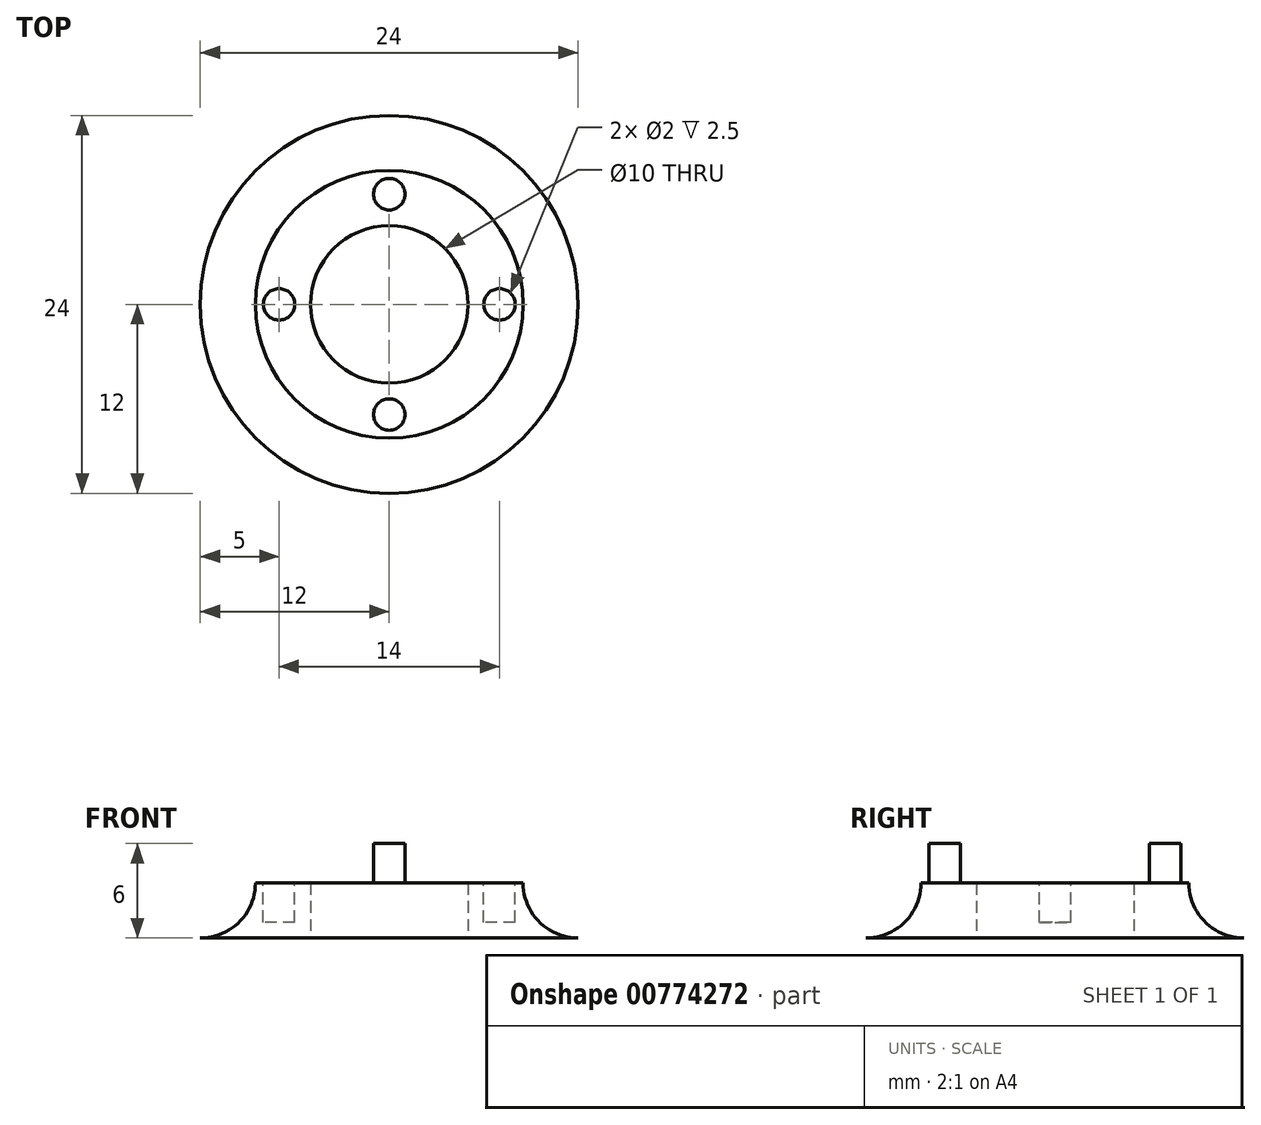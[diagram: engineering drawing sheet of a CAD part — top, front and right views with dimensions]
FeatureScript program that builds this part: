
annotation { "Feature Type Name" : "Feature", "Feature Type Description" : "" }
export const myFeature = defineFeature(function(context is Context, id is Id, definition is map)
    precondition{}
    {
        {
            var Q0;
            Q0=qCreatedBy(makeId("Front.planeOp"),FACE);
            var sketch = newSketch(context, id + "F0", { "sketchPlane" : qUnion([Q0])});
            skLineSegment(sketch, "E0.bottom", {"start": v(0, 0) * mm, "end": v(12, 0) * mm});
            skLineSegment(sketch, "E0.top", {"start": v(0, -3.5) * mm, "end": v(12, -3.5) * mm});
            skLineSegment(sketch, "E0.left", {"start": v(0, 0) * mm, "end": v(0, -3.5) * mm});
            skLineSegment(sketch, "E0.right", {"start": v(12, 0) * mm, "end": v(12, -3.5) * mm});
            skCircle(sketch, "E1", {"center": v(12, 0) * mm, "radius": 3.5 * mm});
            skLineSegment(sketch, "E2.bottom", {"start": v(0, 0) * mm, "end": v(5, 0) * mm});
            skLineSegment(sketch, "E2.top", {"start": v(0, -3.5) * mm, "end": v(5, -3.5) * mm});
            skLineSegment(sketch, "E2.right", {"start": v(5, 0) * mm, "end": v(5, -3.5) * mm});
            skLineSegment(sketch, "E3", {"start": v(0, 0) * mm, "end": v(0, 21.41) * mm});
            skSolve(sketch);
        }
        {
            var Q0;
            {var subQ0=sQuery(id+"F0.wireOp",EDGE,"E2.right");Q0=makeQuery(id+"F0.imprint","IMPRINT",FACE,{"disambiguationData":[TD([[makeQuery(id+"F0.imprint","IMPRINT",EDGE,{"derivedFrom":subQ0}),1.0]])]});}
            var Q1;
            Q1=sQuery(id+"F0.wireOp",EDGE,"E3");
            revolve(context, id + "F1", {"surfaceOperationType" : NewSurfaceOperationType.NEW, "entities" : qUnion([Q0]), "axis" : qUnion([Q1]), "revolveType" : RevolveType.FULL});
        }
        {
            var Q0;
            Q0=makeQuery(id+"F1.opRevolve","SWEPT_FACE",FACE,{"disambiguationData":[OSD([sQuery(id+"F0.wireOp",EDGE,"E0.bottom")])]});
            var sketch = newSketch(context, id + "F2", { "sketchPlane" : qUnion([Q0])});
            skArc(sketch, "E4", {"start": v(-1, 6.93) * mm, "mid": v(-4.95, 4.95) * mm, "end": v(-6.93, 1) * mm});
            skCircle(sketch, "E5", {"center": v(0, 7) * mm, "radius": 1 * mm});
            skCircle(sketch, "E6.1.0", {"center": v(-7, 0) * mm, "radius": 1 * mm});
            skCircle(sketch, "E6.2.0", {"center": v(0, -7) * mm, "radius": 1 * mm});
            skCircle(sketch, "E6.3.0", {"center": v(7, 0) * mm, "radius": 1 * mm});
            skArc(sketch, "E7.trimOffspring", {"start": v(-6.93, -1) * mm, "mid": v(-4.95, -4.95) * mm, "end": v(-1, -6.93) * mm});
            skArc(sketch, "E8.trimOffspring", {"start": v(1, -6.93) * mm, "mid": v(4.95, -4.95) * mm, "end": v(6.93, -1) * mm});
            skArc(sketch, "E9.trimOffspring", {"start": v(6.93, 1) * mm, "mid": v(4.95, 4.95) * mm, "end": v(1, 6.93) * mm});
            skSolve(sketch);
        }
        {
            var Q0;
            {var subQ0=sQuery(id+"F2.wireOp",EDGE,"E5");var subQ1=makeQuery(id+"F2.imprint","INTERSECT",VERTEX,{"derivedFrom":[sQuery(id+"F2.wireOp",EDGE,"E4"),subQ0]});Q0=makeQuery(id+"F2.imprint","IMPRINT",FACE,{"disambiguationData":[TD([[makeQuery(id+"F2.imprint","IMPRINT",EDGE,{"disambiguationData":[TD([[subQ1,-1.0]])],"derivedFrom":subQ0}),1.0]])]});}
            var Q1;
            {var subQ0=sQuery(id+"F2.wireOp",EDGE,"E6.1.0");var subQ1=makeQuery(id+"F2.imprint","INTERSECT",VERTEX,{"derivedFrom":[sQuery(id+"F2.wireOp",EDGE,"E4"),subQ0]});Q1=makeQuery(id+"F2.imprint","IMPRINT",FACE,{"disambiguationData":[TD([[makeQuery(id+"F2.imprint","IMPRINT",EDGE,{"disambiguationData":[TD([[subQ1,1.0]])],"derivedFrom":subQ0}),1.0]])]});}
            var Q2;
            {var subQ0=sQuery(id+"F2.wireOp",EDGE,"E6.2.0");var subQ1=makeQuery(id+"F2.imprint","INTERSECT",VERTEX,{"derivedFrom":[subQ0,sQuery(id+"F2.wireOp",EDGE,"E7.trimOffspring")]});Q2=makeQuery(id+"F2.imprint","IMPRINT",FACE,{"disambiguationData":[TD([[makeQuery(id+"F2.imprint","IMPRINT",EDGE,{"disambiguationData":[TD([[subQ1,1.0]])],"derivedFrom":subQ0}),1.0]])]});}
            var Q3;
            {var subQ0=sQuery(id+"F2.wireOp",EDGE,"E6.3.0");var subQ1=makeQuery(id+"F2.imprint","INTERSECT",VERTEX,{"derivedFrom":[subQ0,sQuery(id+"F2.wireOp",EDGE,"E8.trimOffspring")]});Q3=makeQuery(id+"F2.imprint","IMPRINT",FACE,{"disambiguationData":[TD([[makeQuery(id+"F2.imprint","IMPRINT",EDGE,{"disambiguationData":[TD([[subQ1,1.0]])],"derivedFrom":subQ0}),1.0]])]});}
            extrude(context, id + "F3", {"entities" : qUnion([Q0, Q1, Q2, Q3]), "operationType" : NewBodyOperationType.REMOVE, "oppositeDirection" : true, "depth" : 2.5 * mm, "offsetDistance" : 25 * mm});
        }
        {
            var Q0;
            Q0=makeQuery(id+"F3.boolean.opBoolean","COPY",FACE,{"derivedFrom":makeQuery(id+"F3.opExtrude","CAP_FACE",FACE,{"disambiguationData":[OSD([sQuery(id+"F2.wireOp",EDGE,"E5")])],"isStart":false})});
            var Q1;
            Q1=makeQuery(id+"F3.boolean.opBoolean","COPY",FACE,{"derivedFrom":makeQuery(id+"F3.opExtrude","CAP_FACE",FACE,{"disambiguationData":[OSD([sQuery(id+"F2.wireOp",EDGE,"E6.2.0")])],"isStart":false})});
            extrude(context, id + "F4", {"entities" : qUnion([Q0, Q1]), "operationType" : NewBodyOperationType.ADD, "depth" : 5 * mm, "offsetDistance" : 25 * mm});
        }
    });
